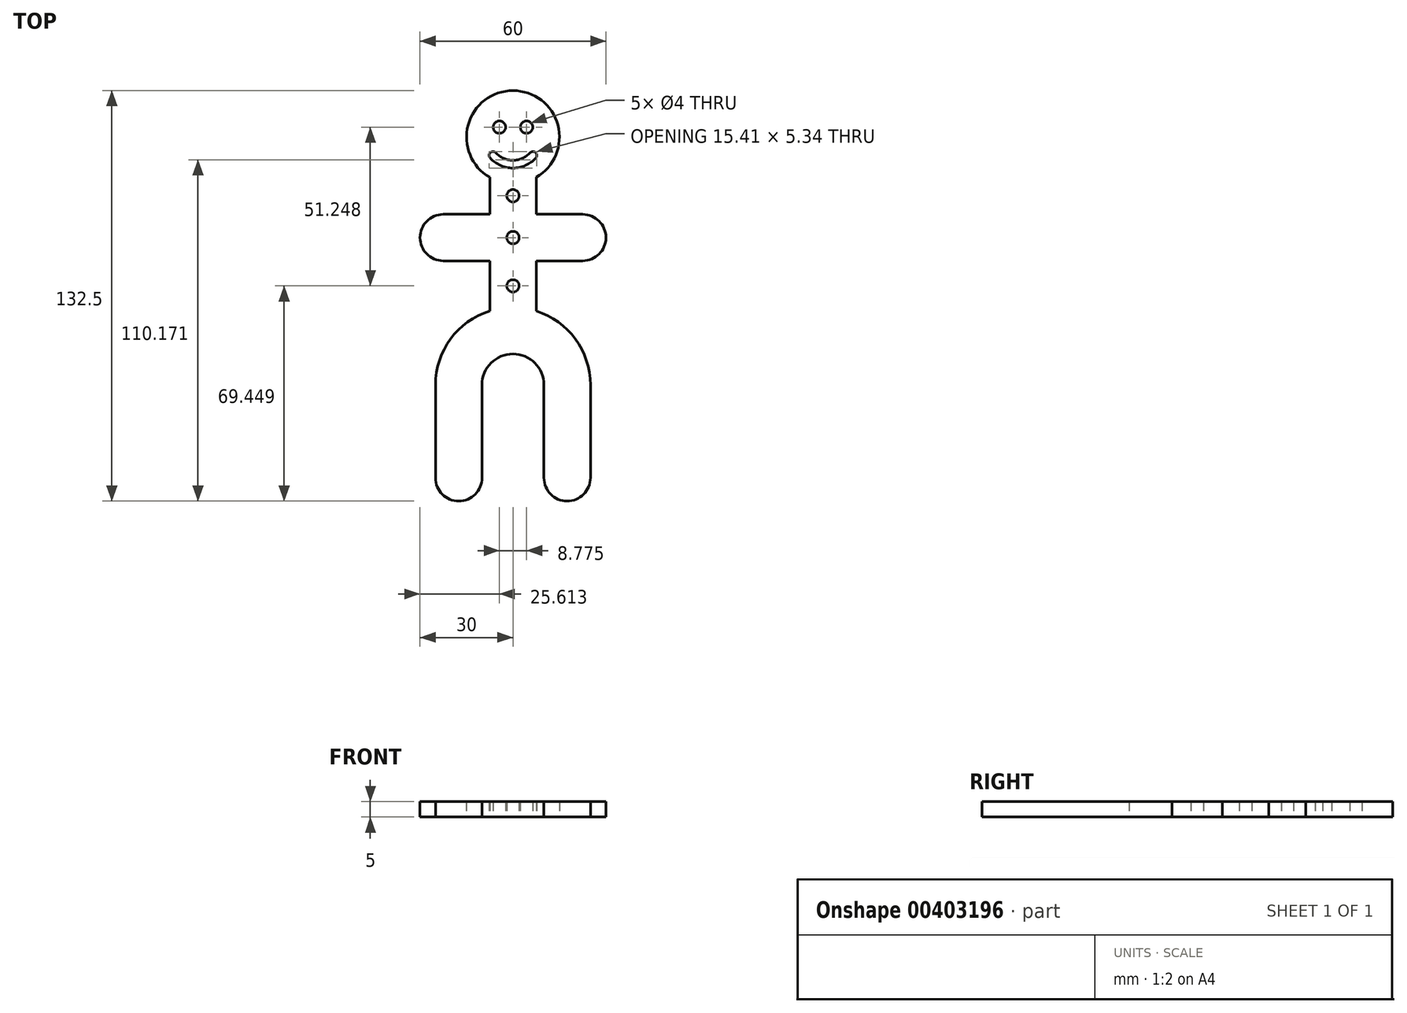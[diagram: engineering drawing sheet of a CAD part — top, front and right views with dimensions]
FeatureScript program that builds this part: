
annotation { "Feature Type Name" : "Feature", "Feature Type Description" : "" }
export const myFeature = defineFeature(function(context is Context, id is Id, definition is map)
    precondition{}
    {
        {
            var Q0;
            Q0=qCreatedBy(makeId("Top.planeOp"),FACE);
            var sketch = newSketch(context, id + "F0", { "sketchPlane" : qUnion([Q0])});
            skArc(sketch, "E0", {"start": v(0, 15) * mm, "mid": v(-14.49, 3.88) * mm, "end": v(-7.5, -13) * mm});
            skLineSegment(sketch, "E1", {"start": v(0, 0) * mm, "end": v(0, -70) * mm, "construction": true});
            skArc(sketch, "E2", {"start": v(0, -70) * mm, "mid": v(-7.07, -72.93) * mm, "end": v(-10, -80) * mm});
            skLineSegment(sketch, "E3", {"start": v(-10, -80) * mm, "end": v(-10, -110) * mm});
            skLineSegment(sketch, "E4.0", {"start": v(-25, -80) * mm, "end": v(-25, -110) * mm});
            skArc(sketch, "E5", {"start": v(-25, -110) * mm, "mid": v(-17.5, -117.5) * mm, "end": v(-10, -110) * mm});
            skArc(sketch, "E6.0", {"start": v(-7.5, -56.15) * mm, "mid": v(-20.16, -65.2) * mm, "end": v(-25, -80) * mm});
            skLineSegment(sketch, "E7.0", {"start": v(-7.5, -13) * mm, "end": v(-7.5, -24.95) * mm});
            skLineSegment(sketch, "E8", {"start": v(0, 0) * mm, "end": v(0, 15) * mm, "construction": true});
            skLineSegment(sketch, "E9", {"start": v(-7.5, -24.95) * mm, "end": v(-22.5, -24.95) * mm});
            skLineSegment(sketch, "E10.0", {"start": v(-7.5, -39.95) * mm, "end": v(-22.5, -39.95) * mm});
            skArc(sketch, "E11", {"start": v(-22.5, -24.95) * mm, "mid": v(-30, -32.45) * mm, "end": v(-22.5, -39.95) * mm});
            skLineSegment(sketch, "E12.trimOffspring", {"start": v(-7.5, -39.95) * mm, "end": v(-7.5, -56.15) * mm});
            skArc(sketch, "E13.MirrorCS", {"start": v(0, 15) * mm, "mid": v(14.49, 3.88) * mm, "end": v(7.5, -13) * mm});
            skLineSegment(sketch, "E14.MirrorCS", {"start": v(7.5, -39.95) * mm, "end": v(7.5, -56.15) * mm});
            skArc(sketch, "E15.MirrorCS", {"start": v(25, -110) * mm, "mid": v(17.5, -117.5) * mm, "end": v(10, -110) * mm});
            skLineSegment(sketch, "E16.MirrorCS", {"start": v(7.5, -24.95) * mm, "end": v(22.5, -24.95) * mm});
            skLineSegment(sketch, "E17.MirrorCS", {"start": v(7.5, -39.95) * mm, "end": v(22.5, -39.95) * mm});
            skLineSegment(sketch, "E18.MirrorCS", {"start": v(25, -80) * mm, "end": v(25, -110) * mm});
            skArc(sketch, "E19.MirrorCS", {"start": v(0, -70) * mm, "mid": v(7.07, -72.93) * mm, "end": v(10, -80) * mm});
            skArc(sketch, "E20.MirrorCS", {"start": v(22.5, -24.95) * mm, "mid": v(30, -32.45) * mm, "end": v(22.5, -39.95) * mm});
            skLineSegment(sketch, "E21.MirrorCS", {"start": v(10, -80) * mm, "end": v(10, -110) * mm});
            skLineSegment(sketch, "E22.MirrorCS", {"start": v(7.5, -13) * mm, "end": v(7.5, -24.95) * mm});
            skArc(sketch, "E23.MirrorCS", {"start": v(7.5, -56.15) * mm, "mid": v(20.16, -65.2) * mm, "end": v(25, -80) * mm});
            skArc(sketch, "E24", {"start": v(-7.38, -6.75) * mm, "mid": v(0, -10) * mm, "end": v(7.38, -6.75) * mm});
            skArc(sketch, "E25", {"start": v(-5.53, -5.06) * mm, "mid": v(0, -7.5) * mm, "end": v(5.53, -5.06) * mm});
            skArc(sketch, "E26", {"start": v(-5.53, -5.06) * mm, "mid": v(-7.3, -4.98) * mm, "end": v(-7.38, -6.75) * mm});
            skArc(sketch, "E27.MirrorCS", {"start": v(5.53, -5.06) * mm, "mid": v(7.3, -4.98) * mm, "end": v(7.38, -6.75) * mm});
            skCircle(sketch, "E28", {"center": v(-4.39, 3.2) * mm, "radius": 2 * mm});
            skCircle(sketch, "E29.MirrorC", {"center": v(4.39, 3.2) * mm, "radius": 2 * mm});
            skLineSegment(sketch, "E30", {"start": v(-11.3, -18.91) * mm, "end": v(13.54, -18.97) * mm, "construction": true});
            skPoint(sketch, "E30.endSnap0", {"position": v(7.5, -18.97) * mm});
            skLineSegment(sketch, "E31", {"start": v(-22.5, -32.45) * mm, "end": v(22.5, -32.45) * mm, "construction": true});
            skLineSegment(sketch, "E32", {"start": v(-7.5, -48.05) * mm, "end": v(7.5, -48.05) * mm, "construction": true});
            skCircle(sketch, "E33", {"center": v(0, -18.94) * mm, "radius": 2 * mm});
            skCircle(sketch, "E34", {"center": v(0, -32.45) * mm, "radius": 2 * mm});
            skCircle(sketch, "E35", {"center": v(0, -48.05) * mm, "radius": 2 * mm});
            skSolve(sketch);
        }
        {
            var Q0;
            Q0=makeQuery(id+"F0.imprint","IMPRINT",FACE,{"disambiguationData":[TD([[makeQuery(id+"F0.imprint","IMPRINT",EDGE,{"derivedFrom":sQuery(id+"F0.wireOp",EDGE,"E0")}),1.0]])]});
            extrude(context, id + "F1", {"entities" : qUnion([Q0]), "depth" : 5 * mm});
        }
    });
